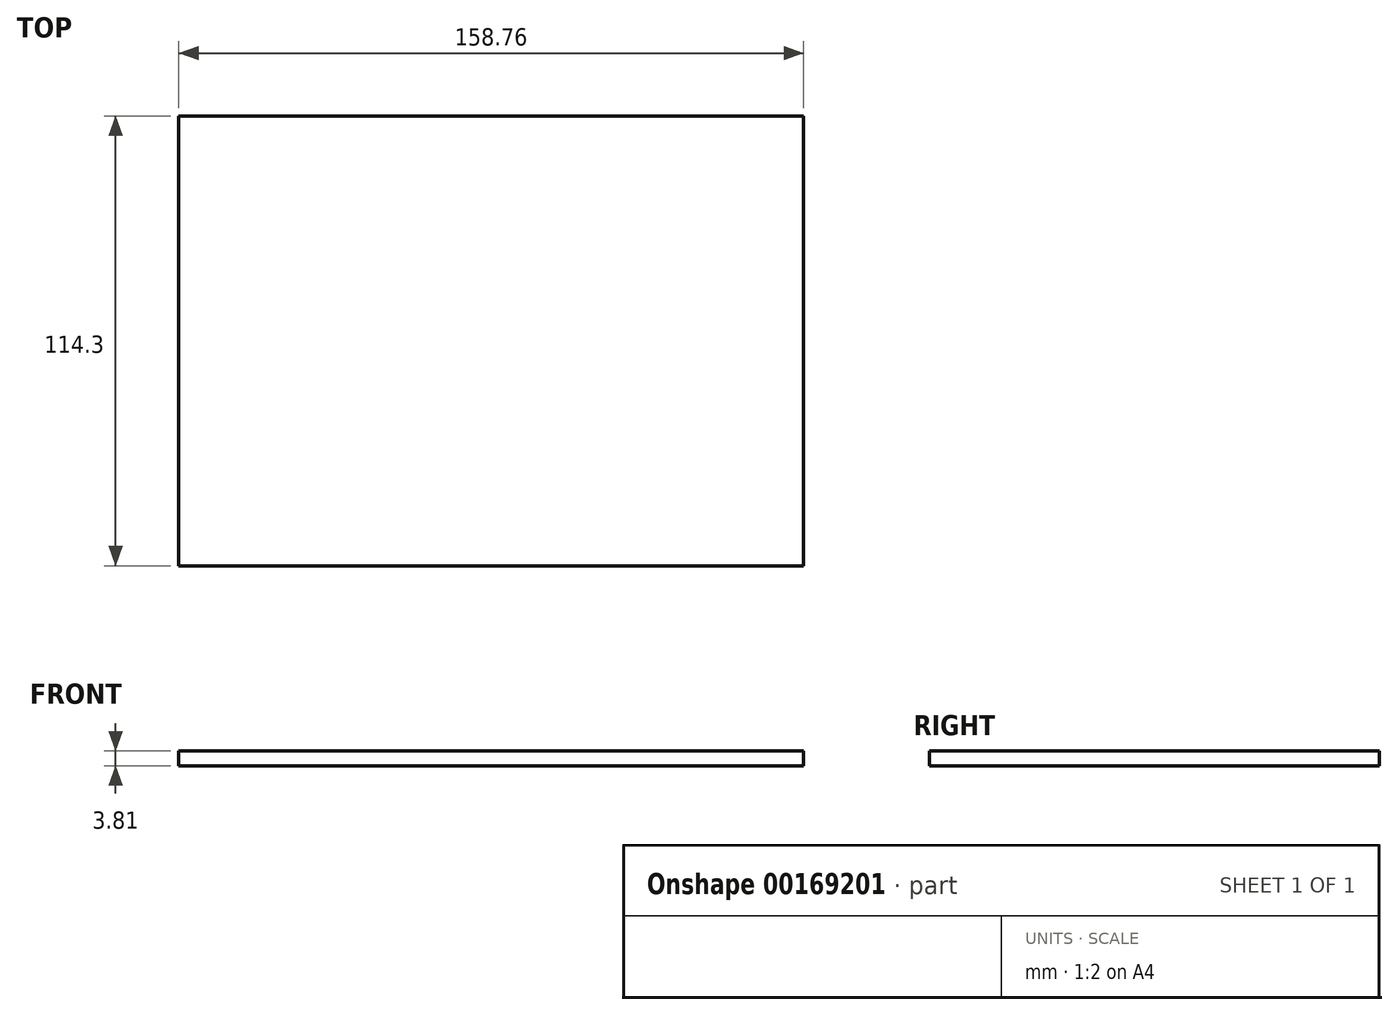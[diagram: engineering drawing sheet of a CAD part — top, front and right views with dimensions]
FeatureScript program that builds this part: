
annotation { "Feature Type Name" : "Feature", "Feature Type Description" : "" }
export const myFeature = defineFeature(function(context is Context, id is Id, definition is map)
    precondition{}
    {
        {
            var Q0;
            Q0=qCreatedBy(makeId("Top.planeOp"),FACE);
            var sketch = newSketch(context, id + "F0", { "sketchPlane" : qUnion([Q0])});
            skLineSegment(sketch, "E0.bottom", {"start": v(79.38, -57.15) * mm, "end": v(-79.38, -57.15) * mm});
            skLineSegment(sketch, "E0.top", {"start": v(79.37, 57.15) * mm, "end": v(-79.38, 57.15) * mm});
            skLineSegment(sketch, "E0.left", {"start": v(79.38, -57.15) * mm, "end": v(79.37, 57.15) * mm});
            skLineSegment(sketch, "E0.right", {"start": v(-79.37, -57.15) * mm, "end": v(-79.38, 57.15) * mm});
            skPoint(sketch, "E0.middle", {"position": v(0, 0) * mm});
            skSolve(sketch);
        }
        {
            var Q0;
            Q0 = qSketchRegion(id + "F0", true);
            extrude(context, id + "F1", {"entities" : qUnion([Q0]), "depth" : 3.8 * mm});
        }
    });
